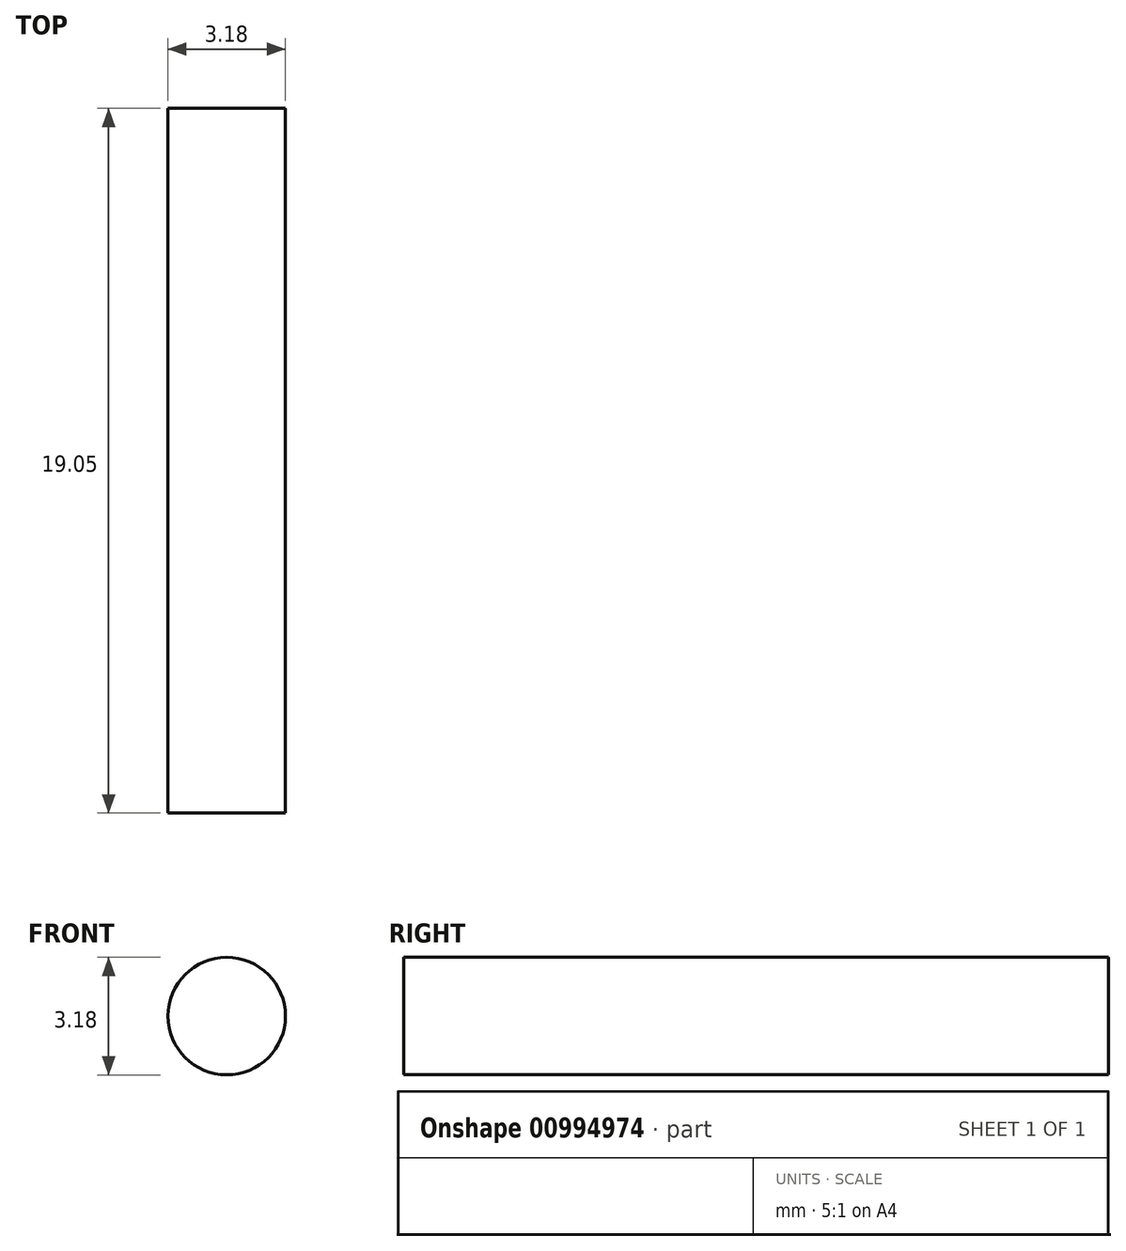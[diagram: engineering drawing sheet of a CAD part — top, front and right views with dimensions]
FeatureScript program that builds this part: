
annotation { "Feature Type Name" : "Feature", "Feature Type Description" : "" }
export const myFeature = defineFeature(function(context is Context, id is Id, definition is map)
    precondition{}
    {
        {
            var Q0;
            Q0=qCreatedBy(makeId("Front.planeOp"),FACE);
            var sketch = newSketch(context, id + "F0", { "sketchPlane" : qUnion([Q0])});
            skCircle(sketch, "E0", {"center": v(0, 0) * mm, "radius": 1.59 * mm});
            skSolve(sketch);
        }
        {
            var Q0;
            Q0=makeQuery(id+"F0.imprint","IMPRINT",FACE,{"disambiguationData":[TD([[makeQuery(id+"F0.imprint","IMPRINT",EDGE,{"derivedFrom":sQuery(id+"F0.wireOp",EDGE,"E0")}),1.0]])]});
            extrude(context, id + "F1", {"entities" : qUnion([Q0]), "depth" : 19.05 * mm, "offsetDistance" : 25.4 * mm});
        }
    });
